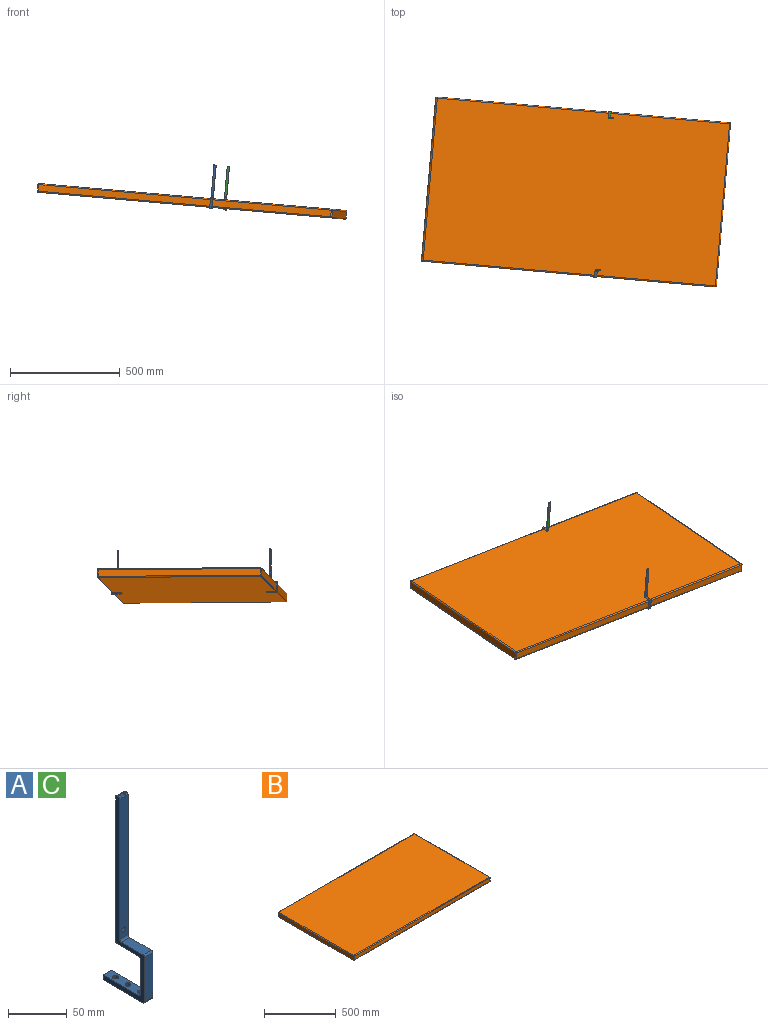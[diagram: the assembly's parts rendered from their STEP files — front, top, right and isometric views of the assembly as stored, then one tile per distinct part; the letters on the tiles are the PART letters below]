
ASSEMBLY  parts=3 mates=5
PART A: 28 faces, bbox 10x50x200 mm
  f0: plane 2.5x1mm, normal (0,0,1), area 2.5mm2, adj f11,f14,f23,f24
  f1: plane 150x10mm, normal (0,1,0), area 1479.3mm2, adj f11,f12,f13,f14,f18,f22,f23
  f2: plane 10x5mm, normal (0,1,0), area 50mm2, adj f3,f10,f11,f12
  f3: plane 43x10mm, normal (0,0,1), area 371.1mm2, adj f2,f11,f12,f15,f16,f17,f20
  f4: plane 37x10mm, normal (0,1,0), area 370mm2, adj f11,f12,f20,f21
  f5: plane 26x10mm, normal (0,0,-1), area 260mm2, adj f11,f12,f21,f22
  f6: plane 2.5x1mm, normal (0,0,1), area 2.5mm2, adj f12,f14,f18,f19
  f7: plane 146x10mm, normal (0,-1,0), area 1439.3mm2, adj f11,f12,f13,f14,f19,f24,f25
  f8: plane 26x10mm, normal (0,0,1), area 260mm2, adj f11,f12,f25,f26
  f9: plane 46x10mm, normal (0,-1,0), area 460mm2, adj f11,f12,f26,f27
  f10: plane 48x10mm, normal (0,0,-1), area 421.1mm2, adj f2,f11,f12,f15,f16,f17,f27
  f11: plane 200x50mm, normal (1,0,0), area 1343.3mm2, adj f0,f1,f2,f3,f4,f5,f7,f8
  f12: plane 200x50mm, normal (-1,0,0), area 1343.3mm2, adj f1,f2,f3,f4,f5,f6,f7,f8
  f13: cylinder r=2.5mm len=5mm, axis (0,-1,0), area 78.5mm2, adj f1,f7
  f14: cylinder r=2.5mm len=5mm, axis (0,-1,0), area 35.7mm2, adj f0,f1,f6,f7,f18,f19,f23,f24
  f15: cylinder r=2.5mm len=5mm, axis (0,0,-1), area 78.5mm2, adj f3,f10
  f16: cylinder r=2.5mm len=5mm, axis (0,0,-1), area 78.5mm2, adj f3,f10
  f17: cylinder r=2.5mm len=5mm, axis (0,0,-1), area 78.5mm2, adj f3,f10
  f18: cylinder r=2mm len=3.5mm, axis (-1,0,0), area 8.5mm2, adj f1,f6,f12,f14
  f19: cylinder r=2mm len=3.5mm, axis (-1,0,0), area 8.5mm2, adj f6,f7,f12,f14
  f20: cylinder r=2mm len=10mm, axis (1,0,0), area 31.4mm2, adj f3,f4,f11,f12
  f21: cylinder r=2mm len=10mm, axis (1,0,0), area 31.4mm2, adj f4,f5,f11,f12
  f22: cylinder r=2mm len=10mm, axis (-1,0,0), area 31.4mm2, adj f1,f5,f11,f12
  f23: cylinder r=2mm len=3.5mm, axis (-1,0,0), area 8.5mm2, adj f0,f1,f11,f14
  f24: cylinder r=2mm len=3.5mm, axis (-1,0,0), area 8.5mm2, adj f0,f7,f11,f14
  f25: cylinder r=2mm len=10mm, axis (1,0,0), area 31.4mm2, adj f7,f8,f11,f12
  f26: cylinder r=2mm len=10mm, axis (-1,0,0), area 31.4mm2, adj f8,f9,f11,f12
  f27: cylinder r=2mm len=10mm, axis (-1,0,0), area 31.4mm2, adj f9,f10,f11,f12
PART B: 26 faces, bbox 1350x750x40 mm
  f0: plane 1340x30mm, normal (0,-1,0), area 40200mm2, adj f14,f19,f22,f25
  f1: plane 740x30mm, normal (1,0,0), area 22200mm2, adj f11,f20,f21,f25
  f2: plane 1340x30mm, normal (0,1,0), area 40200mm2, adj f6,f10,f11,f12
  f3: plane 740x30mm, normal (-1,0,0), area 22200mm2, adj f6,f9,f13,f14
  f4: plane 1340x740mm, normal (0,0,1), area 991600mm2, adj f9,f10,f19,f20
  f5: plane 1340x740mm, normal (0,0,-1), area 991600mm2, adj f12,f13,f21,f22
  f6: cylinder r=5mm len=30mm, axis (0,0,-1), area 235.6mm2, adj f2,f3,f7,f8
  f7: sphere r=5mm, area 39.3mm2, adj f6,f9,f10
  f8: sphere r=5mm, area 39.3mm2, adj f6,f12,f13
  f9: cylinder r=5mm len=740mm, axis (0,1,0), area 5811.9mm2, adj f3,f4,f7,f15
  f10: cylinder r=5mm len=1340mm, axis (1,0,0), area 10524.3mm2, adj f2,f4,f7,f16
  f11: cylinder r=5mm len=30mm, axis (0,0,1), area 235.6mm2, adj f1,f2,f16,f17
  f12: cylinder r=5mm len=1340mm, axis (-1,0,0), area 10524.3mm2, adj f2,f5,f8,f17
  f13: cylinder r=5mm len=740mm, axis (0,-1,0), area 5811.9mm2, adj f3,f5,f8,f18
  f14: cylinder r=5mm len=30mm, axis (0,0,1), area 235.6mm2, adj f0,f3,f15,f18
  f15: sphere r=5mm, area 39.3mm2, adj f9,f14,f19
  f16: sphere r=5mm, area 39.3mm2, adj f10,f11,f20
  f17: sphere r=5mm, area 39.3mm2, adj f11,f12,f21
  f18: sphere r=5mm, area 39.3mm2, adj f13,f14,f22
  f19: cylinder r=5mm len=1340mm, axis (-1,0,0), area 10524.3mm2, adj f0,f4,f15,f23
  f20: cylinder r=5mm len=740mm, axis (0,-1,0), area 5811.9mm2, adj f1,f4,f16,f23
  f21: cylinder r=5mm len=740mm, axis (0,1,0), area 5811.9mm2, adj f1,f5,f17,f24
  f22: cylinder r=5mm len=1340mm, axis (1,0,0), area 10524.3mm2, adj f0,f5,f18,f24
  f23: sphere r=5mm, area 39.3mm2, adj f19,f20,f25
  f24: sphere r=5mm, area 39.3mm2, adj f21,f22,f25
  f25: cylinder r=5mm len=30mm, axis (0,0,-1), area 235.6mm2, adj f0,f1,f23,f24
PART C: same geometry as A
PLACE A rot(axis=(-0.03,0.71,-0.71),7.1deg) t=(48.07,-247.2,15.3)mm
PLACE B rot(axis=(-0.03,0.71,-0.71),7.1deg) t=(-36.28,111.59,28.7)mm
PLACE C rot(axis=(0.04,0,1),175deg) t=(118.77,449.27,9.11)mm
MATE planar A.f5 <-> B.f4  axis (-0.09,0,-1) through (56.17,-257.6,60.77)mm
MATE planar C.f4 <-> B.f2  axis (-0.09,-1,0.01) through (118.2,474.61,34.76)mm
MATE planar C.f12 <-> A.f11  axis (0.99,-0.09,-0.09) through (126.08,454.28,87.67)mm
MATE planar C.f5 <-> B.f4  axis (-0.09,0,-1) through (118.68,459.66,55.3)mm
MATE planar A.f4 <-> B.f0  axis (0.09,1,-0.01) through (46.51,-272.1,22.46)mm
